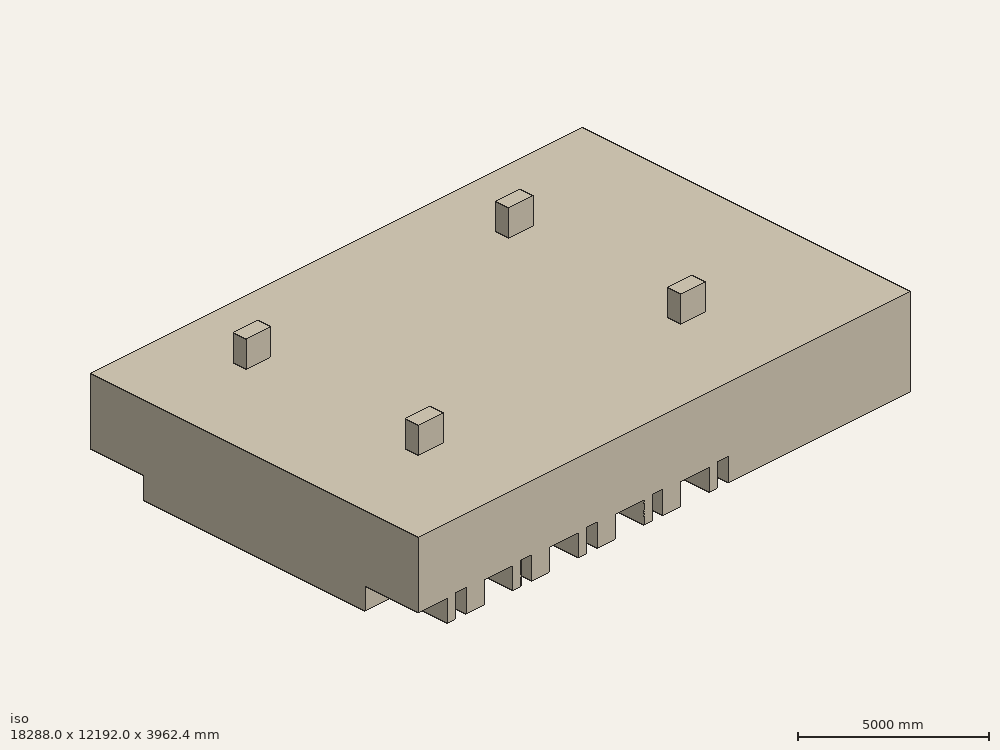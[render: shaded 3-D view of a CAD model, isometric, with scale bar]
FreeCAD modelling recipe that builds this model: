
FCSTD DOCUMENT  (FreeCAD 0.18R14555 (Git shallow))
Label: flow_domain
License: All rights reserved
LicenseURL: http://en.wikipedia.org/wiki/All_rights_reserved
objects: Part::Box×16, Part::MultiFuse×9, Part::Mirroring×1, Part::FeaturePython×1
note: 27 computed .brp shape members not serialized (recipe doc carries the construction recipe); baked Part::Feature solids carry a one-line shape summary decoded from their .brp

FEATURE [Part::Box] Box  label="Room"
  AttacherType = Attacher::AttachEngine3D
  Height = 3048
  Length = 18288
  Width = 12192
FEATURE [Part::Box] Box001  label="Bed 1"
  AttacherType = Attacher::AttachEngine3D
  Height = 762
  Length = 1066.8
  Width = 1981.2
FEATURE [Part::Box] Box002  label="Table 1"
  AttacherType = Attacher::AttachEngine3D
  Height = 798.576
  Length = 396.24
  Placement = pos=(1371.6,0,0) rot=(0,0,1;0rad)
  Width = 396.24
FEATURE [Part::MultiFuse] Fusion  label="Set 1"
  Shapes = -> [Box002,Box001]
FEATURE [Part::Box] Box003  label="Bed 002"
  AttacherType = Attacher::AttachEngine3D
  Height = 762
  Length = 1066.8
  Width = 1981.2
FEATURE [Part::Box] Box004  label="Table 002"
  AttacherType = Attacher::AttachEngine3D
  Height = 798.576
  Length = 396.24
  Placement = pos=(1371.6,0,0) rot=(0,0,1;0rad)
  Width = 396.24
FEATURE [Part::MultiFuse] Fusion001  label="Set 2"
  Placement = pos=(2438.4,0,0) rot=(0,0,1;0rad)
  Shapes = -> [Box004,Box003]
FEATURE [Part::Box] Box005  label="Table 003"
  AttacherType = Attacher::AttachEngine3D
  Height = 798.576
  Length = 396.24
  Placement = pos=(1371.6,0,0) rot=(0,0,1;0rad)
  Width = 396.24
FEATURE [Part::Box] Box006  label="Bed 003"
  AttacherType = Attacher::AttachEngine3D
  Height = 762
  Length = 1066.8
  Width = 1981.2
FEATURE [Part::MultiFuse] Fusion002  label="Set 3"
  Placement = pos=(4876.8,0,0) rot=(0,0,1;0rad)
  Shapes = -> [Box005,Box006]
FEATURE [Part::Box] Box007  label="Bed 004"
  AttacherType = Attacher::AttachEngine3D
  Height = 762
  Length = 1066.8
  Width = 1981.2
FEATURE [Part::Box] Box008  label="Table 004"
  AttacherType = Attacher::AttachEngine3D
  Height = 798.576
  Length = 396.24
  Placement = pos=(1371.6,0,0) rot=(0,0,1;0rad)
  Width = 396.24
FEATURE [Part::MultiFuse] Fusion003  label="Set 4"
  Placement = pos=(7315.2,0,0) rot=(0,0,1;0rad)
  Shapes = -> [Box008,Box007]
FEATURE [Part::Box] Box009  label="Table 005"
  AttacherType = Attacher::AttachEngine3D
  Height = 798.576
  Length = 396.24
  Placement = pos=(1371.6,0,0) rot=(0,0,1;0rad)
  Width = 396.24
FEATURE [Part::Box] Box010  label="Bed 005"
  AttacherType = Attacher::AttachEngine3D
  Height = 762
  Length = 1066.8
  Width = 1981.2
FEATURE [Part::MultiFuse] Fusion004  label="Set 5"
  Placement = pos=(9753.6,0,0) rot=(0,0,1;0rad)
  Shapes = -> [Box009,Box010]
FEATURE [Part::MultiFuse] Fusion005  label="right beds"
  Shapes = -> [Fusion001,Fusion002,Fusion003,Fusion004,Fusion]
FEATURE [Part::Mirroring] Part__Mirroring  label="left beds"
  Base = (0,6096,0)
  Normal = (0,1,0)
  Source = -> Fusion005
FEATURE [Part::Box] Box011  label="Nurse Station"
  AttacherType = Attacher::AttachEngine3D
  Height = 1219.2
  Length = 3048
  Placement = pos=(15240,7620,0) rot=(0,0,1;0rad)
  Width = 4572
FEATURE [Part::Box] Box014  label="Inlet 1"
  AttacherType = Attacher::AttachEngine3D
  Height = 1219.2
  Length = 914.4
  Placement = pos=(12801.6,9448.8,2743.2) rot=(0,0,1;0rad)
  Width = 487.68
FEATURE [Part::Box] Box015  label="Inlet 2"
  AttacherType = Attacher::AttachEngine3D
  Height = 1219.2
  Length = 914.4
  Placement = pos=(12801.6,3048,2743.2) rot=(0,0,1;0rad)
  Width = 487.68
FEATURE [Part::Box] Box018  label="Outlet 2"
  AttacherType = Attacher::AttachEngine3D
  Height = 1219.2
  Length = 914.4
  Placement = pos=(3048,3048,2743.2) rot=(0,0,1;0rad)
  Width = 487.68
FEATURE [Part::Box] Box019  label="Outlet 1"
  AttacherType = Attacher::AttachEngine3D
  Height = 1219.2
  Length = 914.4
  Placement = pos=(3048,9448.8,2743.2) rot=(0,0,1;0rad)
  Width = 487.68
FEATURE [Part::MultiFuse] Fusion006  label="all beds"
  Shapes = -> [Part__Mirroring,Fusion005]
FEATURE [Part::FeaturePython] XOR  label="volume"  # WARN: FeaturePython — macro-defined, semantics opaque (R4)
  Objects = -> [Fusion006,Box,Box011]
  Tolerance = 0
FEATURE [Part::MultiFuse] Fusion007  label="vents"
  Shapes = -> [Box014,Box015,Box018,Box019]
FEATURE [Part::MultiFuse] Fusion008  label="flow_field"
  Shapes = -> [Fusion007,XOR]
